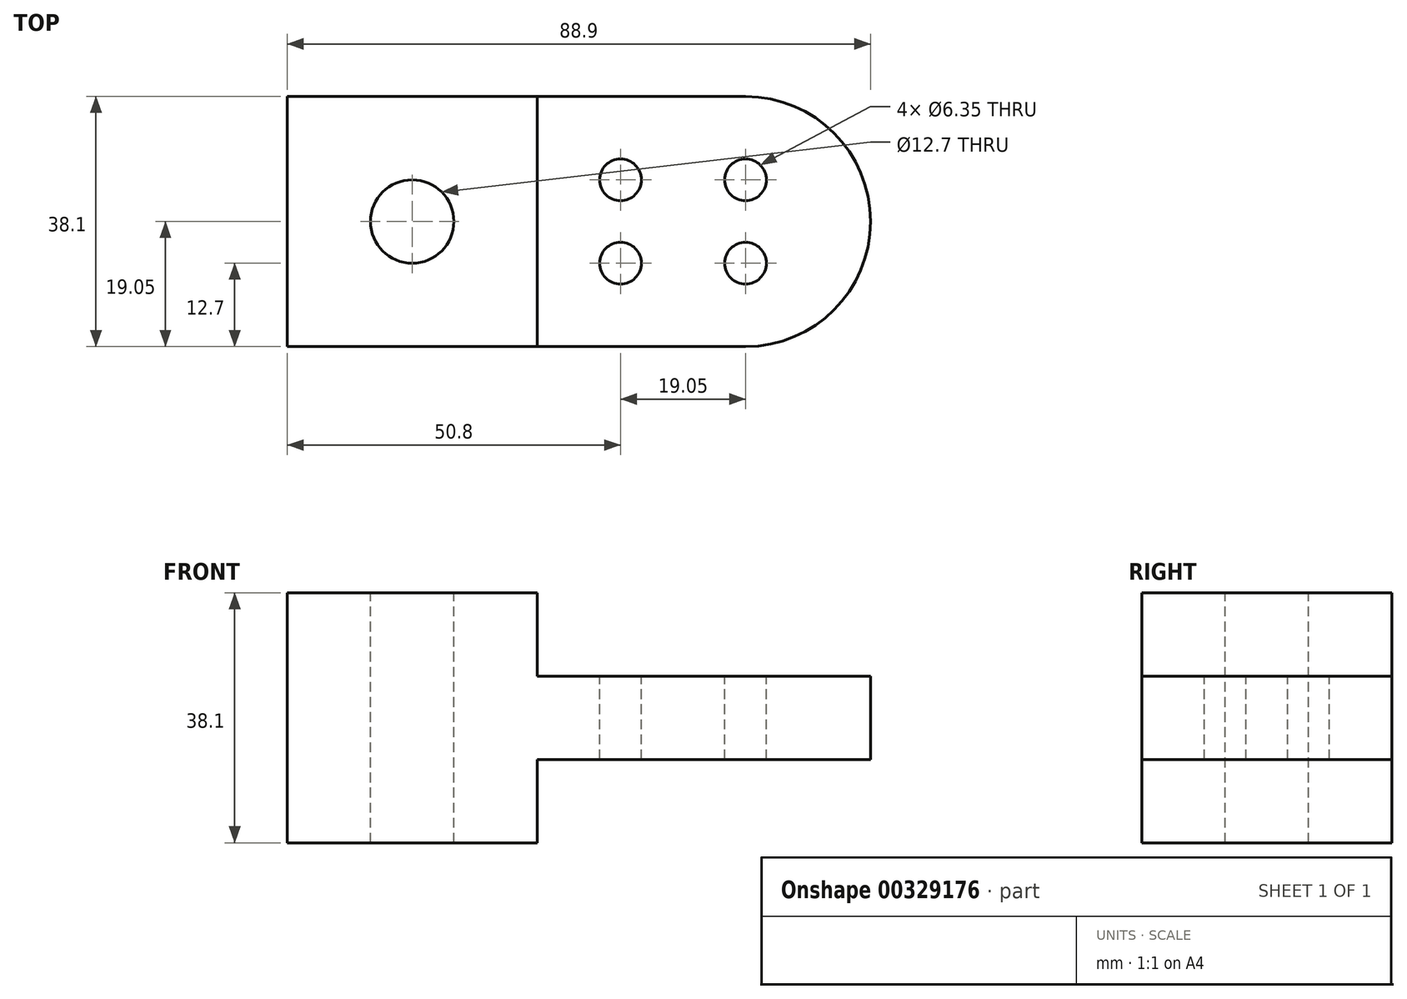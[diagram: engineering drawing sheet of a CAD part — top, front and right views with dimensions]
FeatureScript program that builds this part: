
annotation { "Feature Type Name" : "Feature", "Feature Type Description" : "" }
export const myFeature = defineFeature(function(context is Context, id is Id, definition is map)
    precondition{}
    {
        {
            var Q0;
            Q0=qCreatedBy(makeId("Front.planeOp"),FACE);
            var sketch = newSketch(context, id + "F0", { "sketchPlane" : qUnion([Q0])});
            skLineSegment(sketch, "E0", {"start": v(0, 0) * mm, "end": v(0, 38.1) * mm});
            skLineSegment(sketch, "E1", {"start": v(0, 38.1) * mm, "end": v(38.1, 38.1) * mm});
            skLineSegment(sketch, "E2", {"start": v(38.1, 38.1) * mm, "end": v(38.1, 25.4) * mm});
            skLineSegment(sketch, "E3", {"start": v(38.1, 25.4) * mm, "end": v(88.9, 25.4) * mm});
            skLineSegment(sketch, "E4", {"start": v(88.9, 25.4) * mm, "end": v(88.9, 12.7) * mm});
            skLineSegment(sketch, "E5", {"start": v(88.9, 12.7) * mm, "end": v(38.1, 12.7) * mm});
            skLineSegment(sketch, "E6", {"start": v(38.1, 12.7) * mm, "end": v(38.1, 0) * mm});
            skLineSegment(sketch, "E7", {"start": v(38.1, 0) * mm, "end": v(0, 0) * mm});
            skSolve(sketch);
        }
        {
            var Q0;
            Q0 = qSketchRegion(id + "F0", true);
            extrude(context, id + "F1", {"entities" : qUnion([Q0]), "depth" : 38.1 * mm});
        }
        {
            var Q0;
            Q0=makeQuery(id+"F1.opExtrude","CAP_EDGE",EDGE,{"disambiguationData":[OSD([sQuery(id+"F0.wireOp",EDGE,"E4")])],"isStart":true});
            var Q1;
            Q1=makeQuery(id+"F1.opExtrude","CAP_EDGE",EDGE,{"disambiguationData":[OSD([sQuery(id+"F0.wireOp",EDGE,"E4")])],"isStart":false});
            fillet(context, id + "F2", {"entities" : qUnion([Q0, Q1]), "radius" : 19.05 * mm, "tangentPropagation" : true, "allowEdgeOverflow" : false});
        }
        {
            var Q0;
            Q0=makeQuery(id+"F1.opExtrude","SWEPT_FACE",FACE,{"disambiguationData":[OSD([sQuery(id+"F0.wireOp",EDGE,"E1")])]});
            var sketch = newSketch(context, id + "F3", { "sketchPlane" : qUnion([Q0])});
            skCircle(sketch, "E8", {"center": v(19.05, -19.05) * mm, "radius": 6.35 * mm});
            skLineSegment(sketch, "E9", {"start": v(19.05, -19.05) * mm, "end": v(19.05, 0) * mm, "construction": true});
            skLineSegment(sketch, "E10", {"start": v(19.05, -38.1) * mm, "end": v(19.05, -19.05) * mm, "construction": true});
            skLineSegment(sketch, "E11", {"start": v(19.05, -19.05) * mm, "end": v(0, -19.05) * mm, "construction": true});
            skLineSegment(sketch, "E12", {"start": v(0, -19.05) * mm, "end": v(19.05, -19.05) * mm, "construction": true});
            skLineSegment(sketch, "E13", {"start": v(19.05, -19.05) * mm, "end": v(38.1, -19.05) * mm, "construction": true});
            skCircle(sketch, "E14", {"center": v(50.8, -12.7) * mm, "radius": 3.18 * mm});
            skCircle(sketch, "E15.0.1.0", {"center": v(50.8, -25.4) * mm, "radius": 3.18 * mm});
            skCircle(sketch, "E15.1.0.0", {"center": v(69.85, -12.7) * mm, "radius": 3.18 * mm});
            skCircle(sketch, "E15.1.1.0", {"center": v(69.85, -25.4) * mm, "radius": 3.18 * mm});
            skLineSegment(sketch, "E15.direction1", {"start": v(50.8, -12.7) * mm, "end": v(69.85, -12.7) * mm, "construction": true});
            skLineSegment(sketch, "E15.direction2", {"start": v(50.8, -12.7) * mm, "end": v(50.8, -25.4) * mm, "construction": true});
            skSolve(sketch);
        }
        {
            var Q0;
            Q0 = qSketchRegion(id + "F3", true);
            extrude(context, id + "F4", {"entities" : qUnion([Q0]), "operationType" : NewBodyOperationType.REMOVE, "endBound" : BoundingType.THROUGH_ALL, "oppositeDirection" : true, "depth" : 25.4 * mm});
        }
    });
